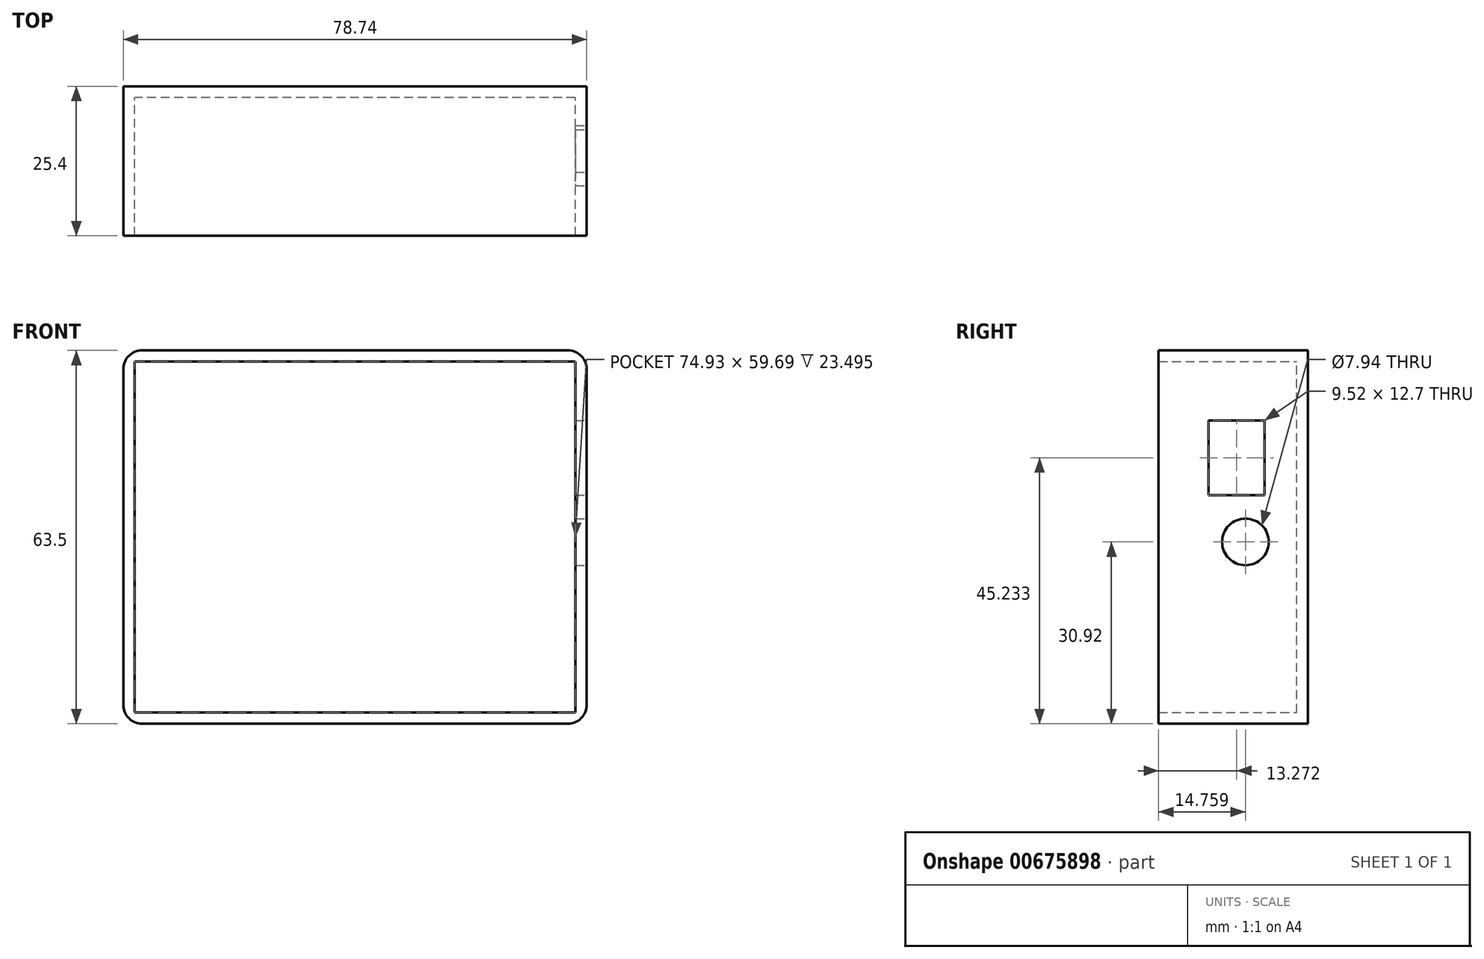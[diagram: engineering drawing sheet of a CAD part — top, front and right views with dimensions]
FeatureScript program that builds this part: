
annotation { "Feature Type Name" : "Feature", "Feature Type Description" : "" }
export const myFeature = defineFeature(function(context is Context, id is Id, definition is map)
    precondition{}
    {
        {
            var Q0;
            Q0=qCreatedBy(makeId("Front.planeOp"),FACE);
            var sketch = newSketch(context, id + "F0", { "sketchPlane" : qUnion([Q0])});
            skLineSegment(sketch, "E0.bottom", {"start": v(0, 0) * mm, "end": v(-78.74, 0) * mm});
            skLineSegment(sketch, "E0.top", {"start": v(0, 63.5) * mm, "end": v(-78.74, 63.5) * mm});
            skLineSegment(sketch, "E0.left", {"start": v(0, 0) * mm, "end": v(0, 63.5) * mm});
            skLineSegment(sketch, "E0.right", {"start": v(-78.74, 0) * mm, "end": v(-78.74, 63.5) * mm});
            skSolve(sketch);
        }
        {
            var Q0;
            Q0 = qSketchRegion(id + "F0", true);
            extrude(context, id + "F1", {"entities" : qUnion([Q0]), "depth" : 25.4 * mm, "offsetDistance" : 25.4 * mm});
        }
        {
            var Q0;
            Q0=makeQuery(id+"F1.opExtrude","CAP_FACE",FACE,{"disambiguationData":[OSD([sQuery(id+"F0.wireOp",EDGE,"E0.bottom"),sQuery(id+"F0.wireOp",EDGE,"E0.top"),sQuery(id+"F0.wireOp",EDGE,"E0.left"),sQuery(id+"F0.wireOp",EDGE,"E0.right")])],"isStart":false});
            shell(context, id + "F2", {"entities" : qUnion([Q0]), "thickness" : 1.9 * mm});
        }
        {
            var Q0;
            Q0=qCreatedBy(makeId("Right.planeOp"),FACE);
            var sketch = newSketch(context, id + "F3", { "sketchPlane" : qUnion([Q0])});
            skPoint(sketch, "E1", {"position": v(-10.64, 30.92) * mm});
            skSolve(sketch);
        }
        {
            var Q0;
            Q0=sQuery(id+"F3.wireOp",VERTEX,"E1");
            var Q1;
            Q1=makeQuery(id+"F1.opExtrude","SWEPT_BODY",BODY,{"disambiguationData":[OSD([sQuery(id+"F0.wireOp",EDGE,"E0.bottom"),sQuery(id+"F0.wireOp",EDGE,"E0.top"),sQuery(id+"F0.wireOp",EDGE,"E0.left"),sQuery(id+"F0.wireOp",EDGE,"E0.right")])]});
            hole(context, id + "F4", {"style" : HoleStyle.SIMPLE, "endStyle" : HoleEndStyle.BLIND, "holeDiameter" : 7.94 * mm, "majorDiameter" : 6.35 * mm, "holeDepth" : 12.7 * mm, "isTappedThrough" : true, "tappedDepth" : 12.7 * mm, "tapClearance" : 3, "locations" : qUnion([Q0]), "scope" : qUnion([Q1])});
        }
        {
            var Q0;
            Q0=qCreatedBy(makeId("Right.planeOp"),FACE);
            var sketch = newSketch(context, id + "F5", { "sketchPlane" : qUnion([Q0])});
            skLineSegment(sketch, "E2.bottom", {"start": v(-16.9, 51.58) * mm, "end": v(-7.37, 51.58) * mm});
            skLineSegment(sketch, "E2.top", {"start": v(-16.9, 38.88) * mm, "end": v(-7.37, 38.88) * mm});
            skLineSegment(sketch, "E2.left", {"start": v(-16.9, 51.58) * mm, "end": v(-16.9, 38.88) * mm});
            skLineSegment(sketch, "E2.right", {"start": v(-7.37, 51.58) * mm, "end": v(-7.37, 38.88) * mm});
            skSolve(sketch);
        }
        {
            var Q0;
            Q0 = qSketchRegion(id + "F5", true);
            extrude(context, id + "F6", {"entities" : qUnion([Q0]), "operationType" : NewBodyOperationType.REMOVE, "oppositeDirection" : true, "depth" : 25.4 * mm, "offsetDistance" : 25.4 * mm});
        }
        {
            var Q0;
            Q0=makeQuery(id+"F1.opExtrude","SWEPT_EDGE",EDGE,{"disambiguationData":[OSD([sQuery(id+"F0.wireOp",EDGE,"E0.top"),sQuery(id+"F0.wireOp",EDGE,"E0.right")])]});
            var Q1;
            Q1=makeQuery(id+"F1.opExtrude","SWEPT_EDGE",EDGE,{"disambiguationData":[OSD([sQuery(id+"F0.wireOp",EDGE,"E0.top"),sQuery(id+"F0.wireOp",EDGE,"E0.left")])]});
            var Q2;
            Q2=makeQuery(id+"F1.opExtrude","SWEPT_EDGE",EDGE,{"disambiguationData":[OSD([sQuery(id+"F0.wireOp",EDGE,"E0.bottom"),sQuery(id+"F0.wireOp",EDGE,"E0.left")])]});
            var Q3;
            Q3=makeQuery(id+"F1.opExtrude","SWEPT_EDGE",EDGE,{"disambiguationData":[OSD([sQuery(id+"F0.wireOp",EDGE,"E0.bottom"),sQuery(id+"F0.wireOp",EDGE,"E0.right")])]});
            fillet(context, id + "F7", {"entities" : qUnion([Q0, Q1, Q2, Q3]), "radius" : 3.17 * mm, "tangentPropagation" : true, "allowEdgeOverflow" : false});
        }
    });
